# Revit family: FILTRATION ANTI-BACTERIENNE
name_source: partatom
category: Equipement de génie climatique
revit_build: Autodesk Revit 2018 (Build: 20170223_1515(x64)
units: mm (PartAtom-declared; Revit-internal decimal feet)

## family parameters
Basée sur le plan de construction = Non
Classification = Aucun
Cote de connecteur circulaire = Utiliser le diamètre
Couper avec des vides une fois chargée = Non
Partagée = Non
Point de calcul de pièce = Non
Toujours verticalement = Oui
Type d'élément = Normal

## types (5) — shared parameters
VISIBILITE_BOCAL = Oui
zero-valued in all types: HAUTEUR, LARGEUR, LONGUEUR, POIDS(Kg)

## per-type parameters (varying)
| type | HAUT_COUVERCLE | HAUT_POT | HAUT_TETE | LARG_TETE | LONG_TETE | OFFSET_FLECHE | OFFSET_PERC | RAY_POT | RAY_POT_1 | ØORIFICE |
| FD30 | 11 mm  [stored 0.0360892 ft] | 133 mm  [stored 0.436352 ft] | 40 mm  [stored 0.131234 ft] | 43 mm  [stored 0.141076 ft] | 114 mm  [stored 0.374016 ft] | 19 mm  [stored 0.062336 ft] | 151 mm  [stored 0.495407 ft] | 56 mm  [stored 0.183727 ft] | 51 mm | 20 mm  [stored 0.0656168 ft] |
| FD65 | 11 mm  [stored 0.0360892 ft] | 257 mm  [stored 0.843176 ft] | 40 mm  [stored 0.131234 ft] | 43 mm  [stored 0.141076 ft] | 114 mm  [stored 0.374016 ft] | 19 mm  [stored 0.062336 ft] | 277 mm  [stored 0.908793 ft] | 56 mm  [stored 0.183727 ft] | 51 mm | 20 mm  [stored 0.0656168 ft] |
| FD130 | 13 mm | 258 mm  [stored 0.846457 ft] | 46 mm  [stored 0.150919 ft] | 57 mm  [stored 0.187008 ft] | 130 mm  [stored 0.426509 ft] | 30 mm  [stored 0.0984252 ft] | 280 mm  [stored 0.918635 ft] | 65 mm  [stored 0.213255 ft] | 60 mm | 32 mm  [stored 0.104987 ft] |
| FD320 | 48 mm  [stored 0.15748 ft] | 238 mm  [stored 0.78084 ft] | 104 mm | 63 mm  [stored 0.206693 ft] | 180 mm  [stored 0.590551 ft] | 50 mm  [stored 0.164042 ft] | 309.5 mm  [stored 1.01542 ft] | 90 mm  [stored 0.295276 ft] | 85 mm  [stored 0.278871 ft] | 50 mm  [stored 0.164042 ft] |
| FD600 | 48 mm  [stored 0.15748 ft] | 535 mm  [stored 1.75525 ft] | 104 mm | 63 mm  [stored 0.206693 ft] | 180 mm  [stored 0.590551 ft] | 50 mm  [stored 0.164042 ft] | 606.5 mm  [stored 1.98983 ft] | 90 mm  [stored 0.295276 ft] | 85 mm  [stored 0.278871 ft] | 50 mm  [stored 0.164042 ft] |

note: [stored X ft] marks values corroborated as IEEE doubles in the binary element streams (Revit-internal decimal feet)
